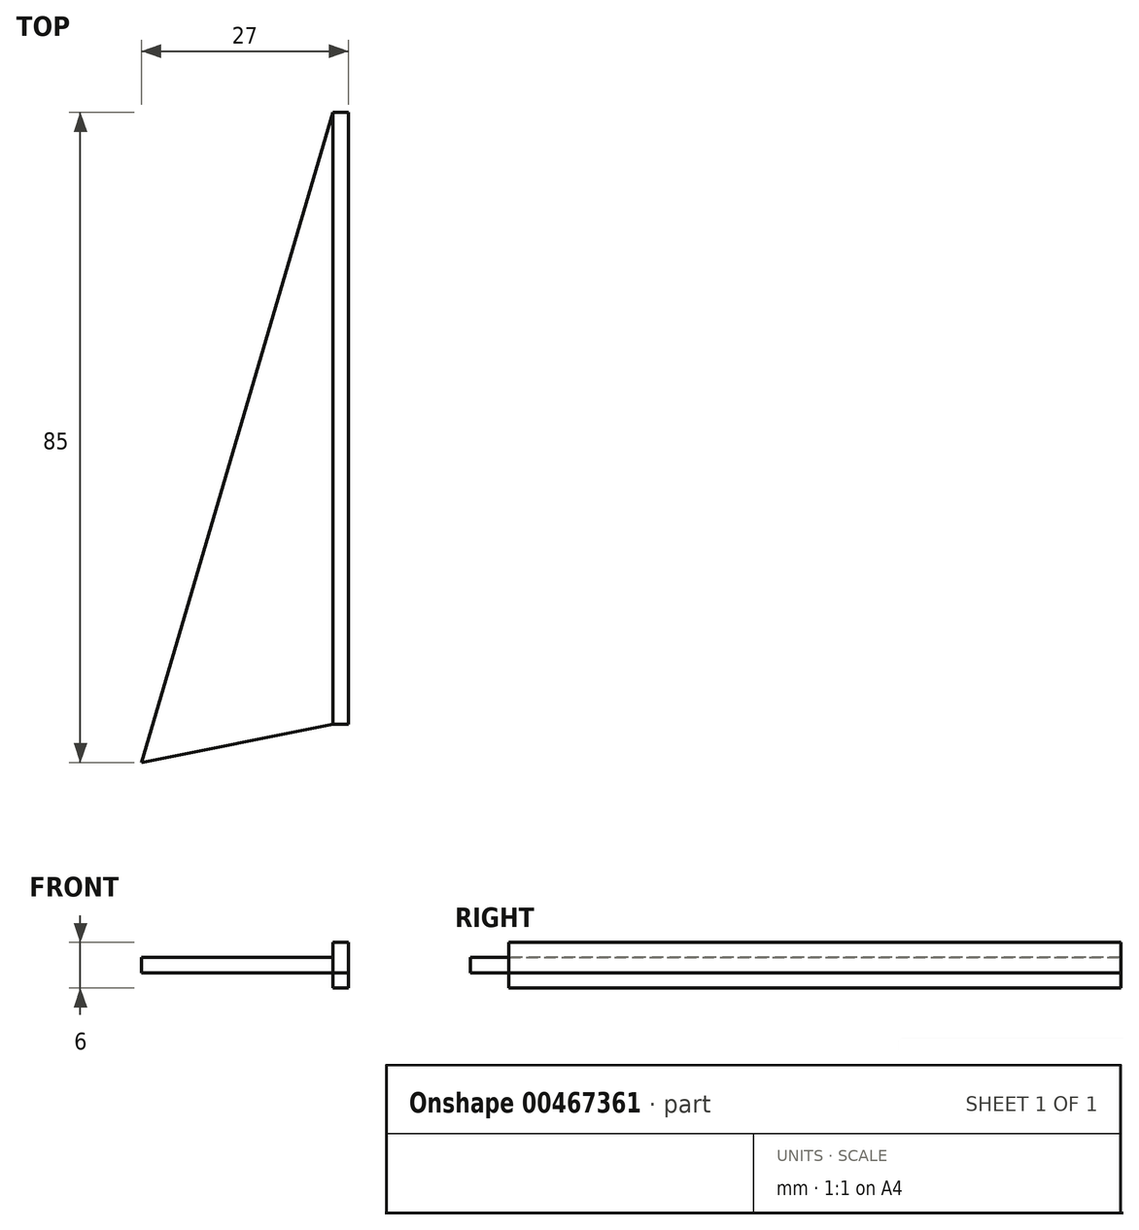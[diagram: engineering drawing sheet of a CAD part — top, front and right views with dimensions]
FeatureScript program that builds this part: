
annotation { "Feature Type Name" : "Feature", "Feature Type Description" : "" }
export const myFeature = defineFeature(function(context is Context, id is Id, definition is map)
    precondition{}
    {
        {
            var Q0;
            Q0=qCreatedBy(makeId("Top.planeOp"),FACE);
            var sketch = newSketch(context, id + "F0", { "sketchPlane" : qUnion([Q0])});
            skLineSegment(sketch, "E0", {"start": v(0, 0) * mm, "end": v(0, 80) * mm});
            skLineSegment(sketch, "E1", {"start": v(0, 80) * mm, "end": v(-25, -5) * mm});
            skLineSegment(sketch, "E2", {"start": v(-25, -5) * mm, "end": v(0, 0) * mm});
            skSolve(sketch);
        }
        {
            var Q0;
            Q0=makeQuery(id+"F0.imprint","IMPRINT",FACE,{"disambiguationData":[TD([[makeQuery(id+"F0.imprint","IMPRINT",EDGE,{"derivedFrom":sQuery(id+"F0.wireOp",EDGE,"E0")}),1.0]])]});
            extrude(context, id + "F1", {"entities" : qUnion([Q0]), "depth" : 2 * mm});
        }
        {
            var Q0;
            Q0=makeQuery(id+"F1.opExtrude","CAP_FACE",FACE,{"disambiguationData":[OSD([sQuery(id+"F0.wireOp",EDGE,"E0"),sQuery(id+"F0.wireOp",EDGE,"E1"),sQuery(id+"F0.wireOp",EDGE,"E2")])],"isStart":true});
            var sketch = newSketch(context, id + "F2", { "sketchPlane" : qUnion([Q0])});
            skLineSegment(sketch, "E3.bottom", {"start": v(0, -80) * mm, "end": v(2, -80) * mm});
            skLineSegment(sketch, "E3.top", {"start": v(0, 0) * mm, "end": v(2, 0) * mm});
            skLineSegment(sketch, "E3.left", {"start": v(0, -80) * mm, "end": v(0, 0) * mm});
            skLineSegment(sketch, "E3.right", {"start": v(2, -80) * mm, "end": v(2, 0) * mm});
            skSolve(sketch);
        }
        {
            var Q0;
            Q0=makeQuery(id+"F2.imprint","IMPRINT",FACE,{"disambiguationData":[TD([[makeQuery(id+"F2.imprint","IMPRINT",EDGE,{"derivedFrom":sQuery(id+"F2.wireOp",EDGE,"E3.bottom")}),1.0]])]});
            extrude(context, id + "F3", {"entities" : qUnion([Q0]), "depth" : 2 * mm});
        }
        {
            var Q0;
            Q0=makeQuery(id+"F3.opExtrude","CAP_FACE",FACE,{"disambiguationData":[OSD([sQuery(id+"F2.wireOp",EDGE,"E3.bottom"),sQuery(id+"F2.wireOp",EDGE,"E3.top"),sQuery(id+"F2.wireOp",EDGE,"E3.left"),sQuery(id+"F2.wireOp",EDGE,"E3.right")])],"isStart":true});
            extrude(context, id + "F4", {"entities" : qUnion([Q0]), "depth" : 4 * mm});
        }
    });
